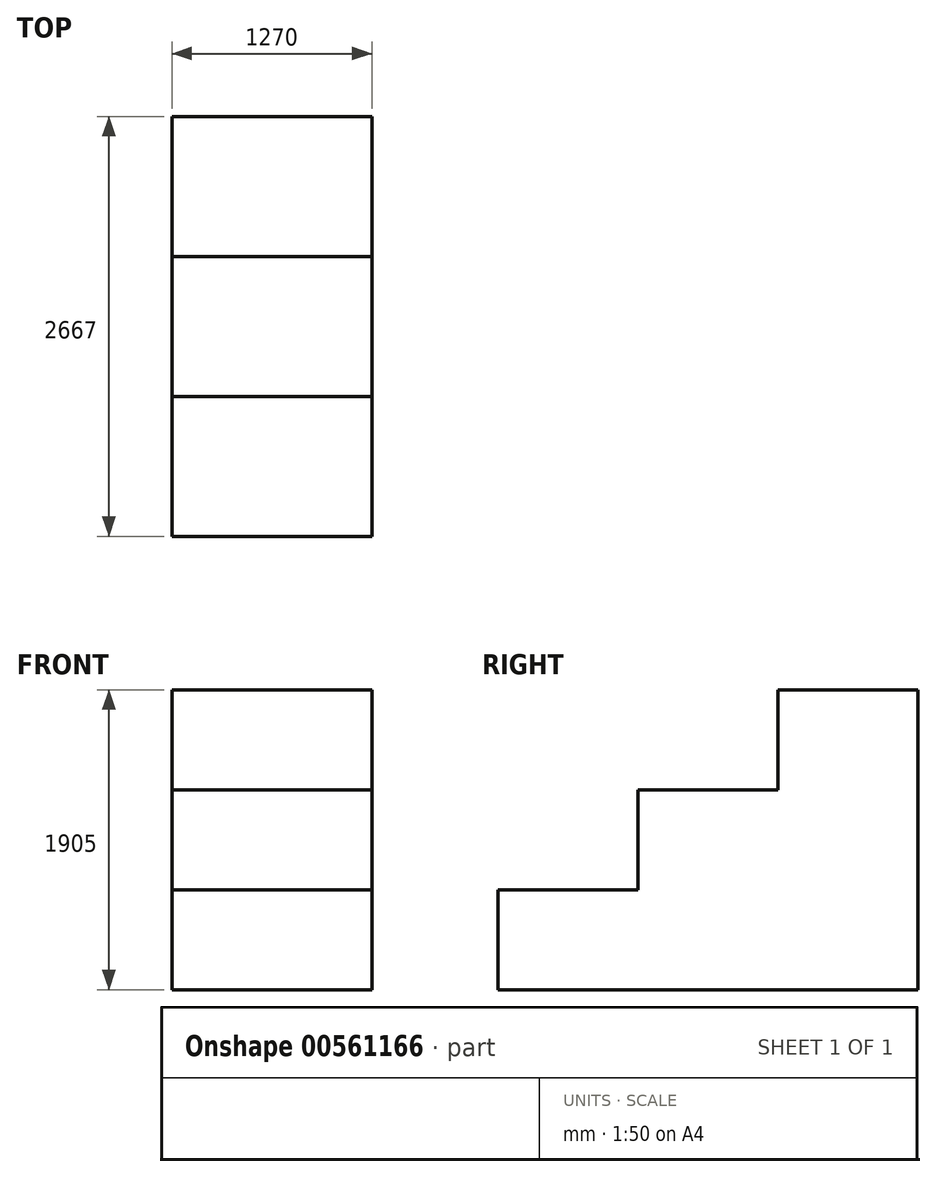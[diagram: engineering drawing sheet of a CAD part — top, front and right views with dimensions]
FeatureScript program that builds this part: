
annotation { "Feature Type Name" : "Feature", "Feature Type Description" : "" }
export const myFeature = defineFeature(function(context is Context, id is Id, definition is map)
    precondition{}
    {
        {
            var Q0;
            Q0=qCreatedBy(makeId("Right.planeOp"),FACE);
            var sketch = newSketch(context, id + "F0", { "sketchPlane" : qUnion([Q0])});
            skLineSegment(sketch, "E0", {"start": v(-1301.46, -720.9) * mm, "end": v(1365.54, -720.9) * mm});
            skLineSegment(sketch, "E1", {"start": v(1365.54, -720.9) * mm, "end": v(1365.54, 1184.1) * mm});
            skLineSegment(sketch, "E2", {"start": v(1365.54, 1184.1) * mm, "end": v(476.54, 1184.1) * mm});
            skLineSegment(sketch, "E3", {"start": v(476.54, 1184.1) * mm, "end": v(476.54, 549.1) * mm});
            skLineSegment(sketch, "E4", {"start": v(476.54, 549.1) * mm, "end": v(-412.46, 549.1) * mm});
            skLineSegment(sketch, "E5", {"start": v(-412.46, 549.1) * mm, "end": v(-412.46, -85.9) * mm});
            skLineSegment(sketch, "E6", {"start": v(-412.46, -85.9) * mm, "end": v(-1301.46, -85.9) * mm});
            skLineSegment(sketch, "E7", {"start": v(-1301.46, -85.9) * mm, "end": v(-1301.46, -720.9) * mm});
            skSolve(sketch);
        }
        {
            var Q0;
            Q0 = qSketchRegion(id + "F0", true);
            extrude(context, id + "F1", {"entities" : qUnion([Q0]), "depth" : 1270 * mm, "offsetDistance" : 25.4 * mm});
        }
    });
